FCSTD DOCUMENT  (FreeCAD 0.17R13541 (Git))
Label: Xtrusion
License: All rights reserved
LicenseURL: http://en.wikipedia.org/wiki/All_rights_reserved
objects: Sketcher::SketchObject×1
note: 1 computed .brp shape members not serialized (recipe doc carries the construction recipe); baked Part::Feature solids carry a one-line shape summary decoded from their .brp

FEATURE [Sketcher::SketchObject] Sketch
  sketch-geometry (24):
    g0: LineSegment StartX=-74.467 StartY=-24.6214 StartZ=0 EndX=-62.563 EndY=-24.6214 EndZ=0
    g1: LineSegment StartX=-62.563 StartY=-24.6214 StartZ=0 EndX=-66.7495 EndY=-20.4348 EndZ=0
    g2: LineSegment StartX=-66.7495 StartY=-20.4348 StartZ=0 EndX=-53.3764 EndY=-20.4348 EndZ=0
    g3: LineSegment StartX=-53.3764 StartY=-20.4348 StartZ=0 EndX=-57.563 EndY=-24.6214 EndZ=0
    g4: LineSegment StartX=-57.563 StartY=-24.6214 StartZ=0 EndX=-45.659 EndY=-24.6214 EndZ=0
    g5: LineSegment StartX=-45.659 StartY=-24.6214 StartZ=0 EndX=-45.659 EndY=-12.7174 EndZ=0
    g6: LineSegment StartX=-45.659 StartY=-12.7174 StartZ=0 EndX=-49.8456 EndY=-16.904 EndZ=0
    g7: LineSegment StartX=-49.8456 StartY=-16.904 StartZ=0 EndX=-49.8456 EndY=-3.53086 EndZ=0
    g8: LineSegment StartX=-49.8456 StartY=-3.53086 StartZ=0 EndX=-45.659 EndY=-7.71741 EndZ=0
    g9: LineSegment StartX=-45.659 StartY=-7.71741 StartZ=0 EndX=-45.659 EndY=4.18655 EndZ=0
    g10: LineSegment StartX=-45.659 StartY=4.18655 StartZ=0 EndX=-57.563 EndY=4.18655 EndZ=0
    g11: LineSegment StartX=-57.563 StartY=4.18655 StartZ=0 EndX=-53.3764 EndY=0 EndZ=0
    g12: LineSegment StartX=-53.3764 StartY=0 StartZ=0 EndX=-66.7495 EndY=0 EndZ=0
    g13: LineSegment StartX=-66.7495 StartY=0 StartZ=0 EndX=-62.563 EndY=4.18655 EndZ=0
    g14: LineSegment StartX=-62.563 StartY=4.18655 StartZ=0 EndX=-74.467 EndY=4.18655 EndZ=0
    g15: LineSegment StartX=-74.467 StartY=4.18655 StartZ=0 EndX=-74.467 EndY=-7.71741 EndZ=0
    g16: LineSegment StartX=-74.467 StartY=-7.71741 StartZ=0 EndX=-70.2804 EndY=-3.53086 EndZ=0
    g17: LineSegment StartX=-70.2804 StartY=-3.53086 StartZ=0 EndX=-70.2804 EndY=-16.904 EndZ=0
    g18: LineSegment StartX=-70.2804 StartY=-16.904 StartZ=0 EndX=-74.467 EndY=-12.7174 EndZ=0
    g19: LineSegment StartX=-74.467 StartY=-12.7174 StartZ=0 EndX=-74.467 EndY=-24.6214 EndZ=0
    g20: LineSegment [constr] StartX=-62.563 StartY=-24.6214 StartZ=0 EndX=-57.563 EndY=-24.6214 EndZ=0
    g21: LineSegment [constr] StartX=-62.563 StartY=4.18655 StartZ=0 EndX=-57.563 EndY=4.18655 EndZ=0
    g22: LineSegment [constr] StartX=-45.659 StartY=-7.71741 StartZ=0 EndX=-45.659 EndY=-12.7174 EndZ=0
    g23: LineSegment [constr] StartX=-74.467 StartY=-7.71741 StartZ=0 EndX=-74.467 EndY=-12.7174 EndZ=0
  constraints (69):
    c: Horizontal(g0)
    c: Coincident(g0,g1)
    c: Coincident(g1,g2)
    c: Horizontal(g2)
    c: Coincident(g2,g3)
    c: Coincident(g3,g4)
    c: Horizontal(g4)
    c: Coincident(g4,g5)
    c: Vertical(g5)
    c: Coincident(g5,g6)
    c: Coincident(g6,g7)
    c: Vertical(g7)
    c: Coincident(g7,g8)
    c: Coincident(g8,g9)
    c: Vertical(g9)
    c: Coincident(g9,g10)
    c: Horizontal(g10)
    c: Coincident(g10,g11)
    c: Coincident(g11,g12)
    c: PointOnObject(g12,g-1)
    c: Horizontal(g12)
    c: Coincident(g12,g13)
    c: Coincident(g13,g14)
    c: Horizontal(g14)
    c: Coincident(g14,g15)
    c: Vertical(g15)
    c: Coincident(g15,g16)
    c: Coincident(g16,g17)
    c: Vertical(g17)
    c: Coincident(g17,g18)
    c: Coincident(g18,g19)
    c: Vertical(g19)
    c: Equal(g14,g10)
    c: Equal(g10,g9)
    c: Equal(g9,g5)
    c: Equal(g5,g4)
    c: Equal(g4,g0)
    c: Equal(g0,g19)
    c: Equal(g19,g15)
    c: Equal(g17,g12)
    c: Equal(g12,g7)
    c: Equal(g7,g2)
    c: Angle(g1,g0) = 0.785398
    c: Angle(g19,g18) = 0.785398
    c: Angle(g4,g3) = 0.785398
    c: Angle(g6,g5) = 0.785398
    c: Angle(g9,g8) = 0.785398
    c: Angle(g11,g10) = 0.785398
    c: Angle(g14,g13) = 0.785398
    c: Angle(g16,g15) = 0.785398
    c: Equal(g16,g13)
    c: Equal(g13,g11)
    c: Equal(g11,g8)
    c: Equal(g8,g6)
    c: Equal(g6,g3)
    c: Equal(g3,g1)
    c: Equal(g1,g18)
    c: Coincident(g20,g0)
    c: Coincident(g20,g3)
    c: Coincident(g21,g13)
    c: Coincident(g21,g10)
    c: Coincident(g22,g8)
    c: Coincident(g22,g5)
    c: Coincident(g23,g15)
    c: Coincident(g23,g18)
    c: Equal(g23,g21)
    c: Equal(g21,g22)
    c: Equal(g22,g20)
    c: Distance(g21) = 5
